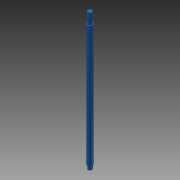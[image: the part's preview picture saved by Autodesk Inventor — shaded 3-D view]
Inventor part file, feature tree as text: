
AUTODESK INVENTOR PART (.ipt)
format: ipt  version: 2015 (Build 190159000, 159)  size: 130,560 bytes
history: native  units: mm
features: extrude x5, sketch x5, plane x2, chamfer x1, pattern_linear x1
ambient origin geometry x8: Origin, YZ Plane, XZ Plane, XY Plane, X Axis, Y Axis, Z Axis, Center Point
bodies: 实体1 (feature_tree)
feature tree (14):
  extrude  "拉伸1"  Depth=450.0mm TaperAngle=0.0deg
  extrude  "拉伸2"  Depth=40.0mm TaperAngle=0.0deg
  extrude  "拉伸3"  Depth=2.0mm TaperAngle=0.0deg
  chamfer  "倒角1"  Distance=2.0mm Angle=45.0deg
  plane  "工作平面1"
  extrude  "拉伸4"  Depth=16.0mm
  pattern_linear  "矩形阵列1"  Spacing1=42.0mm  [1 undecoded]
  plane  "工作平面2"
  extrude  "拉伸5"  Depth=10.0mm TaperAngle=0.0deg
  sketch  "草图1"  dims[d0=20.0mm d1=450.0mm d2=0.0mm]
  sketch  "草图2"  dims[d3=15.0mm d4=40.0mm d5=0.0mm]
  sketch  "草图3"  dims[d6=15.0mm d7=15.0mm d8=0.0mm d9=0.5mm d10=2.0mm d11=45.0deg]
  sketch  "草图4"  dims[d12=6.0mm d13=16.0mm]
  sketch  "草图5"  dims[d14=0.0mm d15=42.0mm d16=2.5mm d17=0.0mm d18=40.0mm d20=120.0mm d21=4.0mm d22=10.0mm d23=13.383017mm d24=1.5mm d25=0.0mm]
note: 1 required parameter value undecoded (feature->parameter linkage not recoverable at this tier; creation-order binding heuristic only, values carry confidence <= 0.55)
